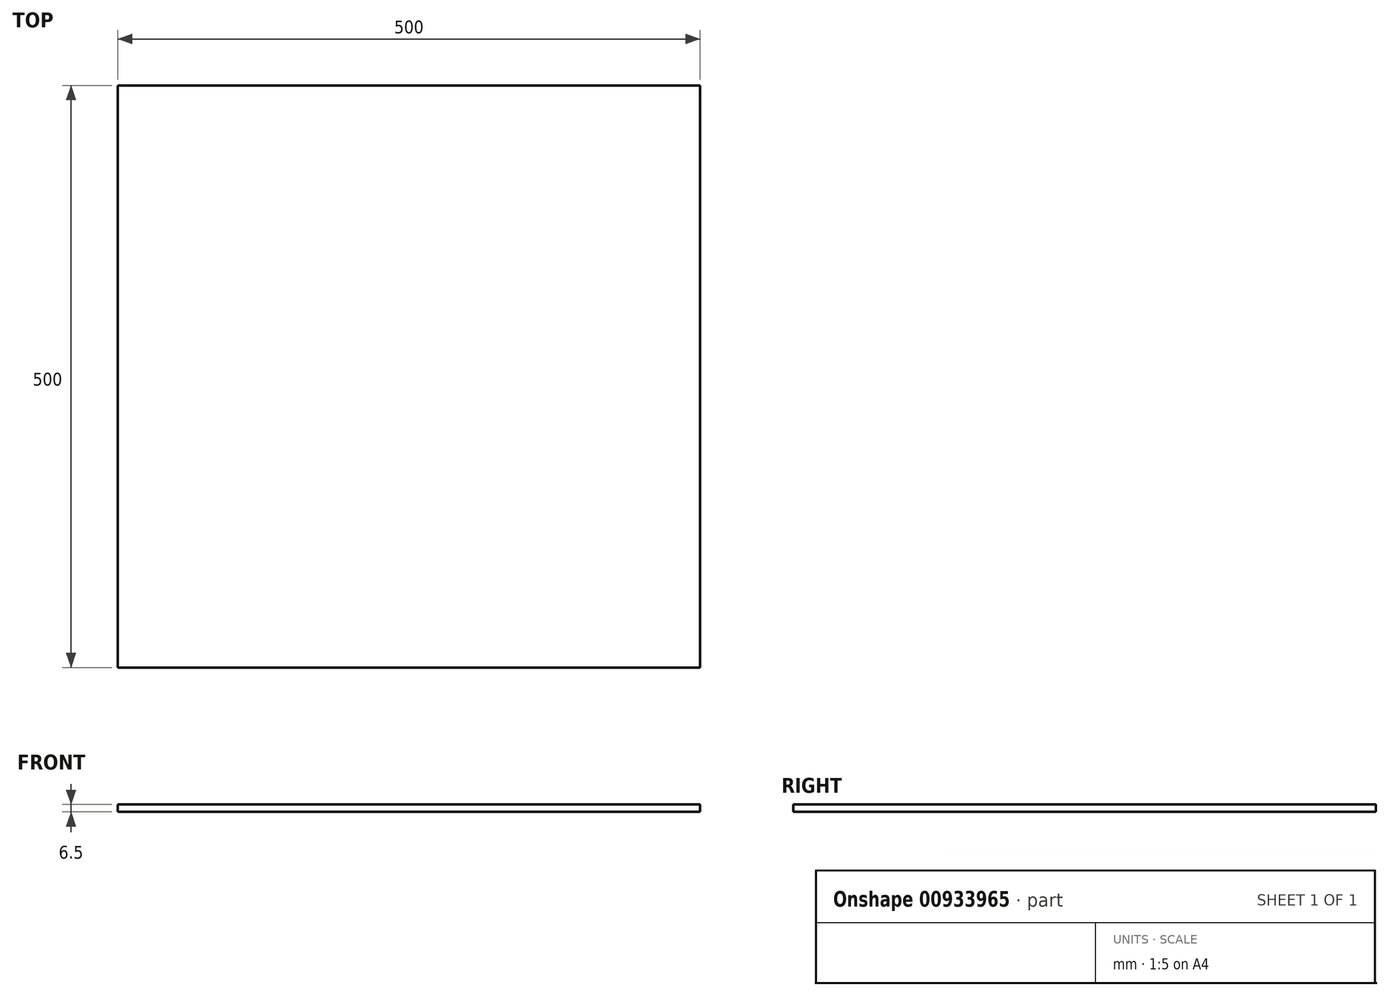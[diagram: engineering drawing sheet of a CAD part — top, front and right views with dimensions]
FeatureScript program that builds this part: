
annotation { "Feature Type Name" : "Feature", "Feature Type Description" : "" }
export const myFeature = defineFeature(function(context is Context, id is Id, definition is map)
    precondition{}
    {
        {
            assignVariable(context, id + "F0", {"name" : "glass_W", "anyValue" : 6.5});
        }
        {
            var Q0;
            Q0=qCreatedBy(makeId("Top.planeOp"),FACE);
            var sketch = newSketch(context, id + "F1", { "sketchPlane" : qUnion([Q0])});
            skLineSegment(sketch, "E0.bottom", {"start": v(-250, 250) * mm, "end": v(250, 250) * mm});
            skLineSegment(sketch, "E0.top", {"start": v(-250, -250) * mm, "end": v(250, -250) * mm});
            skLineSegment(sketch, "E0.left", {"start": v(-250, 250) * mm, "end": v(-250, -250) * mm});
            skLineSegment(sketch, "E0.right", {"start": v(250, 250) * mm, "end": v(250, -250) * mm});
            skPoint(sketch, "E0.middle", {"position": v(0, 0) * mm});
            skSolve(sketch);
        }
        {
            var Q0;
            Q0=makeQuery(id+"F1.imprint","IMPRINT",FACE,{"disambiguationData":[TD([[makeQuery(id+"F1.imprint","IMPRINT",EDGE,{"derivedFrom":sQuery(id+"F1.wireOp",EDGE,"E0.bottom")}),-1.0]])]});
            extrude(context, id + "F2", {"entities" : qUnion([Q0]), "depth" : (getVariable(context, 'glass_W')) * mm, "offsetDistance" : 25 * mm});
        }
    });
